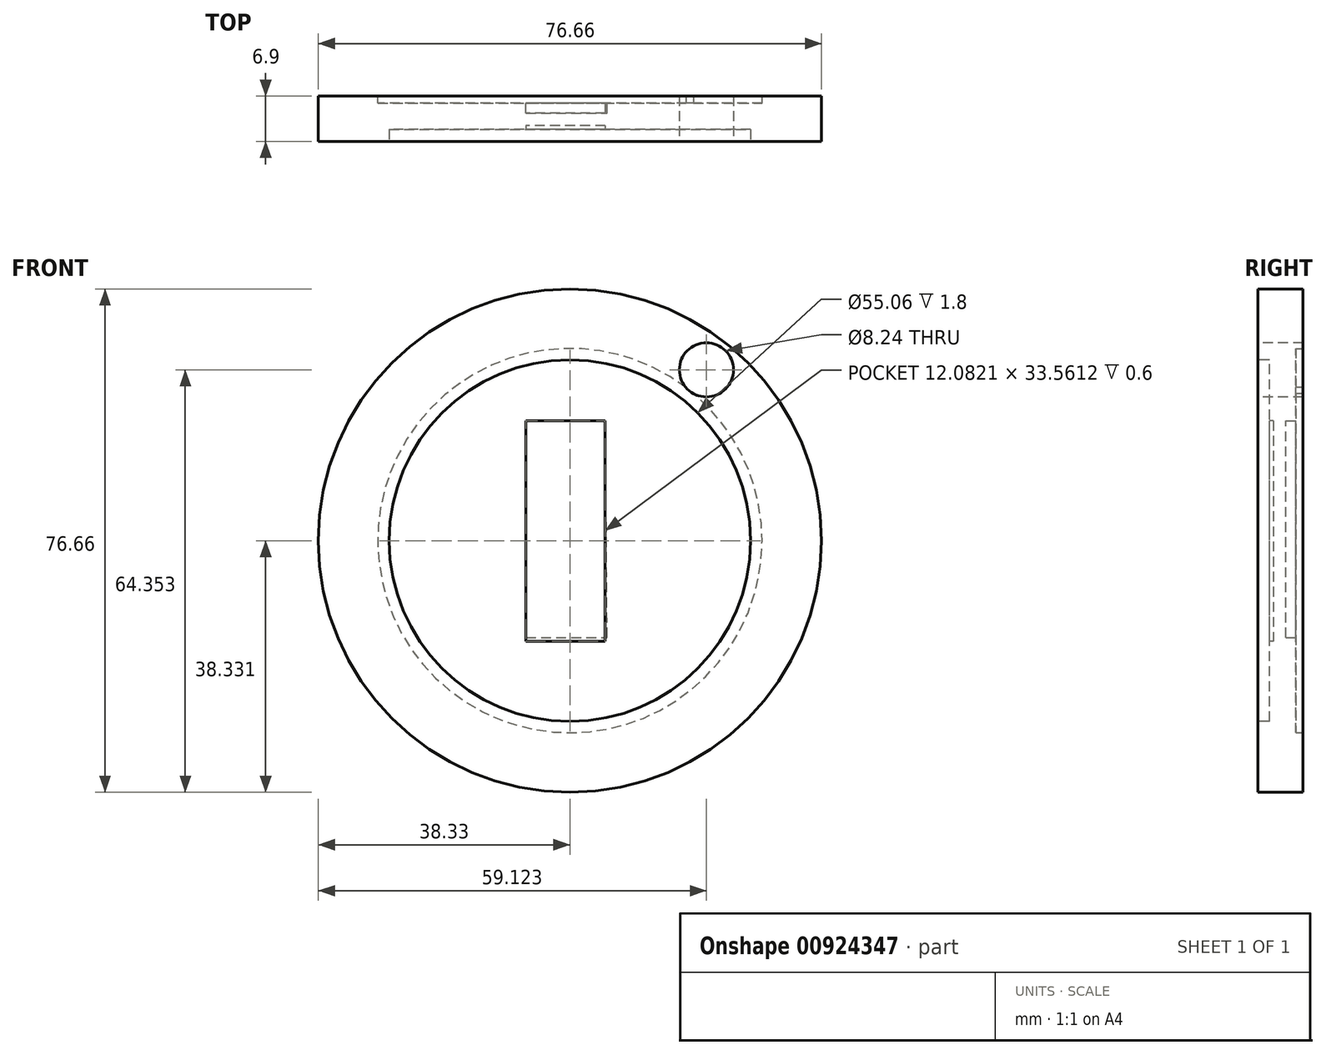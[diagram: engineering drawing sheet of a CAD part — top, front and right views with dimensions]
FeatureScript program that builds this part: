
annotation { "Feature Type Name" : "Feature", "Feature Type Description" : "" }
export const myFeature = defineFeature(function(context is Context, id is Id, definition is map)
    precondition{}
    {
        {
            var Q0;
            Q0=qCreatedBy(makeId("Front.planeOp"),FACE);
            var sketch = newSketch(context, id + "F0", { "sketchPlane" : qUnion([Q0])});
            skCircle(sketch, "E0", {"center": v(-38.26, 38) * mm, "radius": 38.33 * mm});
            skSolve(sketch);
        }
        {
            var Q0;
            Q0=makeQuery(id+"F0.imprint","IMPRINT",FACE,{"disambiguationData":[TD([[makeQuery(id+"F0.imprint","IMPRINT",EDGE,{"derivedFrom":sQuery(id+"F0.wireOp",EDGE,"E0")}),1.0]])]});
            extrude(context, id + "F1", {"entities" : qUnion([Q0]), "depth" : 6.9 * mm, "offsetDistance" : 25.4 * mm});
        }
        {
            var Q0;
            Q0=makeQuery(id+"F1.opExtrude","CAP_FACE",FACE,{"disambiguationData":[OSD([sQuery(id+"F0.wireOp",EDGE,"E0")])],"isStart":false});
            var sketch = newSketch(context, id + "F2", { "sketchPlane" : qUnion([Q0])});
            skCircle(sketch, "E1", {"center": v(-38.26, 38) * mm, "radius": 27.53 * mm});
            skSolve(sketch);
        }
        {
            var Q0;
            Q0=makeQuery(id+"F2.imprint","IMPRINT",FACE,{"disambiguationData":[TD([[makeQuery(id+"F2.imprint","IMPRINT",EDGE,{"derivedFrom":sQuery(id+"F2.wireOp",EDGE,"E1")}),1.0]])]});
            extrude(context, id + "F3", {"entities" : qUnion([Q0]), "operationType" : NewBodyOperationType.REMOVE, "oppositeDirection" : true, "depth" : 1.8 * mm, "offsetDistance" : 25 * mm});
        }
        {
            var Q0;
            Q0=makeQuery(id+"F1.opExtrude","CAP_FACE",FACE,{"disambiguationData":[OSD([sQuery(id+"F0.wireOp",EDGE,"E0")])],"isStart":true});
            var sketch = newSketch(context, id + "F4", { "sketchPlane" : qUnion([Q0])});
            skCircle(sketch, "E2", {"center": v(38.26, 38) * mm, "radius": 29.26 * mm});
            skSolve(sketch);
        }
        {
            var Q0;
            Q0=makeQuery(id+"F4.imprint","IMPRINT",FACE,{"disambiguationData":[TD([[makeQuery(id+"F4.imprint","IMPRINT",EDGE,{"derivedFrom":sQuery(id+"F4.wireOp",EDGE,"E2")}),1.0]])]});
            extrude(context, id + "F5", {"entities" : qUnion([Q0]), "operationType" : NewBodyOperationType.REMOVE, "oppositeDirection" : true, "depth" : 1.1 * mm, "offsetDistance" : 25 * mm});
        }
        {
            var Q0;
            Q0=makeQuery(id+"F3.boolean.opBoolean","COPY",FACE,{"derivedFrom":makeQuery(id+"F3.opExtrude","CAP_FACE",FACE,{"disambiguationData":[OSD([sQuery(id+"F2.wireOp",EDGE,"E1")])],"isStart":false})});
            var sketch = newSketch(context, id + "F6", { "sketchPlane" : qUnion([Q0])});
            skLineSegment(sketch, "E3", {"start": v(-44.97, 56.25) * mm, "end": v(-44.97, 22.69) * mm});
            skLineSegment(sketch, "E4", {"start": v(-44.97, 22.69) * mm, "end": v(-32.9, 22.69) * mm});
            skLineSegment(sketch, "E5", {"start": v(-32.9, 22.69) * mm, "end": v(-32.9, 56.25) * mm});
            skLineSegment(sketch, "E6", {"start": v(-32.9, 56.25) * mm, "end": v(-44.97, 56.25) * mm});
            skSolve(sketch);
        }
        {
            var Q0;
            Q0=makeQuery(id+"F5.boolean.opBoolean","COPY",FACE,{"derivedFrom":makeQuery(id+"F5.opExtrude","CAP_FACE",FACE,{"disambiguationData":[OSD([sQuery(id+"F4.wireOp",EDGE,"E2")])],"isStart":false})});
            var sketch = newSketch(context, id + "F7", { "sketchPlane" : qUnion([Q0])});
            skLineSegment(sketch, "E7", {"start": v(32.87, 56.25) * mm, "end": v(44.95, 56.25) * mm});
            skLineSegment(sketch, "E8", {"start": v(44.95, 56.25) * mm, "end": v(44.95, 23.22) * mm});
            skLineSegment(sketch, "E9", {"start": v(44.95, 23.22) * mm, "end": v(32.6, 23.22) * mm});
            skLineSegment(sketch, "E10", {"start": v(32.6, 23.22) * mm, "end": v(32.87, 56.25) * mm});
            skSolve(sketch);
        }
        {
            var Q0;
            Q0=makeQuery(id+"F7.imprint","IMPRINT",FACE,{"disambiguationData":[TD([[makeQuery(id+"F7.imprint","IMPRINT",EDGE,{"derivedFrom":sQuery(id+"F7.wireOp",EDGE,"E7")}),-1.0]])]});
            extrude(context, id + "F8", {"entities" : qUnion([Q0]), "operationType" : NewBodyOperationType.REMOVE, "oppositeDirection" : true, "depth" : 1.5 * mm, "offsetDistance" : 25 * mm});
        }
        {
            var Q0;
            Q0=makeQuery(id+"F6.imprint","IMPRINT",FACE,{"disambiguationData":[TD([[makeQuery(id+"F6.imprint","IMPRINT",EDGE,{"derivedFrom":sQuery(id+"F6.wireOp",EDGE,"E3")}),1.0]])]});
            extrude(context, id + "F9", {"entities" : qUnion([Q0]), "operationType" : NewBodyOperationType.REMOVE, "oppositeDirection" : true, "depth" : 0.6 * mm, "offsetDistance" : 25 * mm});
        }
        {
            var Q0;
            Q0=makeQuery(id+"F1.opExtrude","CAP_FACE",FACE,{"disambiguationData":[OSD([sQuery(id+"F0.wireOp",EDGE,"E0")])],"isStart":false});
            var sketch = newSketch(context, id + "F10", { "sketchPlane" : qUnion([Q0])});
            skCircle(sketch, "E11", {"center": v(-17.47, 64.01) * mm, "radius": 4.12 * mm});
            skSolve(sketch);
        }
        {
            var Q0;
            Q0=makeQuery(id+"F10.imprint","IMPRINT",FACE,{"disambiguationData":[TD([[makeQuery(id+"F10.imprint","IMPRINT",EDGE,{"derivedFrom":sQuery(id+"F10.wireOp",EDGE,"E11")}),1.0]])]});
            extrude(context, id + "F11", {"entities" : qUnion([Q0]), "operationType" : NewBodyOperationType.REMOVE, "oppositeDirection" : true, "depth" : 25 * mm, "offsetDistance" : 25 * mm});
        }
    });
